AUTODESK INVENTOR PART (.ipt)
format: ipt  version: 2012 SP2 (Build 160219200, 219)  size: 105,984 bytes
history: native  units: in
note: dims shown in document units (in); Inventor stores cm internally (conversion verified against a paired STEP export)
features: sketch x4, extrude x3, reference x3
ambient origin geometry x8: Origin, YZ Plane, XZ Plane, XY Plane, X Axis, Y Axis, Z Axis, Center Point
bodies: Solid1 (feature_tree)
feature tree (10):
  extrude  "Extrusion1"  Depth=0.9843in
  extrude  "Extrusion2"  Depth=0.5906in
  sketch  "Sketch3"  dims[d5=0.254in d6=120.0deg]
  extrude  "Extrusion3"  TaperAngle=120.0deg  [1 undecoded]
  sketch  "Sketch1"  dims[d0=0.3937in d1=0.9843in]
  reference  "Reference1"
  reference  "Reference2"
  sketch  "Sketch2"  dims[d3=3.7402in d4=0.5906in]
  reference  "Reference3"
  sketch  "Sketch4"  dims[d7=0.1705in d8=0.1344in d9=0.0in d10=0.1344in d11=0.3797in d12=0.0in d13=0.0in d14=0.1969in d15=0.0719in d16=0.0in]
note: 1 required parameter value undecoded (feature->parameter linkage not recoverable at this tier; creation-order binding heuristic only, values carry confidence <= 0.55)
